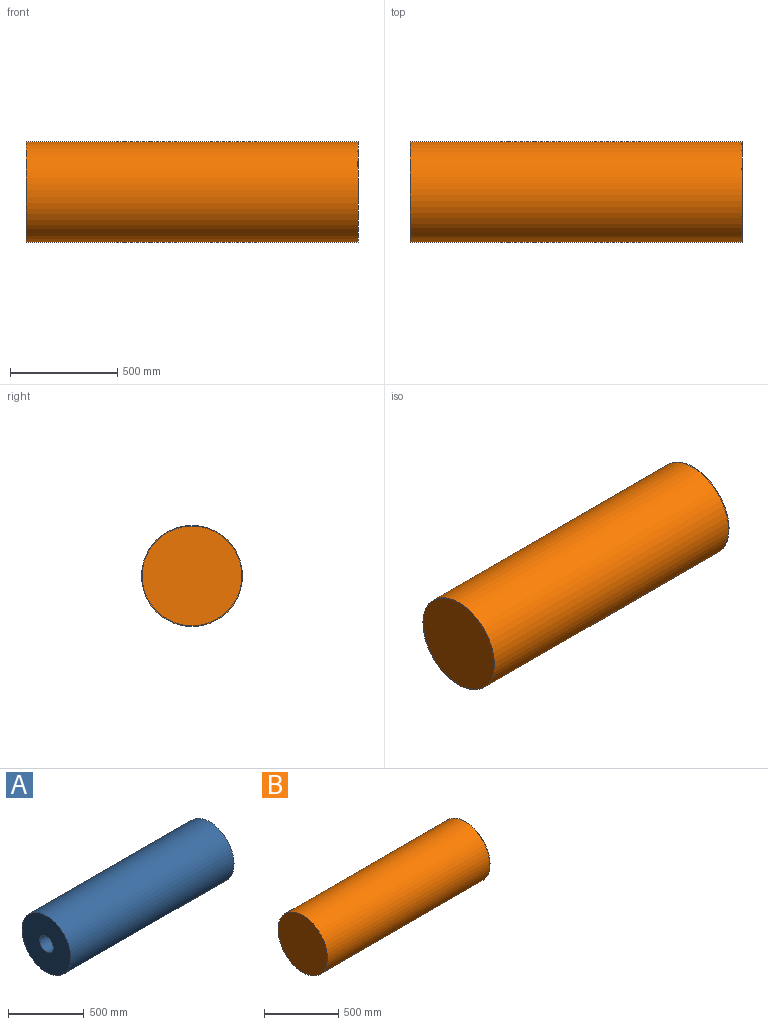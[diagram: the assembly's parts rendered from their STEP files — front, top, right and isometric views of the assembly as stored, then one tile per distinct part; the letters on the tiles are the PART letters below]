
ASSEMBLY  parts=2 mates=1
PART A: 4 faces, bbox 1524x457.2x457.2 mm
  f0: cylinder r=63.5mm len=1524mm, axis (-1,0,0), area 608049mm2, adj f2,f3
  f1: cylinder r=228.6mm len=1524mm, axis (-1,0,0), area 2188976.3mm2, adj f2,f3
  f2: plane 457.2x457.2mm, normal (1,0,0), area 151505.5mm2, adj f0,f1
  f3: plane 457.2x457.2mm, normal (-1,0,0), area 151505.5mm2, adj f0,f1
PART B: 6 faces, bbox 1549.4x471x471 mm
  f0: cylinder r=235.49mm len=1549.4mm, axis (-1,0,0), area 2292527.3mm2, adj f1,f2
  f1: plane 470.98x470.98mm, normal (1,0,0), area 174217.6mm2, adj f0
  f2: plane 470.98x470.98mm, normal (-1,0,0), area 174217.6mm2, adj f0
  f3: cylinder r=232.95mm len=1544.32mm, axis (-1,0,0), area 2260364.5mm2, adj f4,f5
  f4: plane 465.9x465.9mm, normal (-1,0,0), area 170479.6mm2, adj f3
  f5: plane 465.9x465.9mm, normal (1,0,0), area 170479.6mm2, adj f3
PLACE A t=(176.93,-302.76,243.57)mm
PLACE B t=(166.45,-302.92,10.22)mm
MATE parallel B.f0 <-> A.f1  axis (1,0,0) through (1715.85,-302.92,242.62)mm
